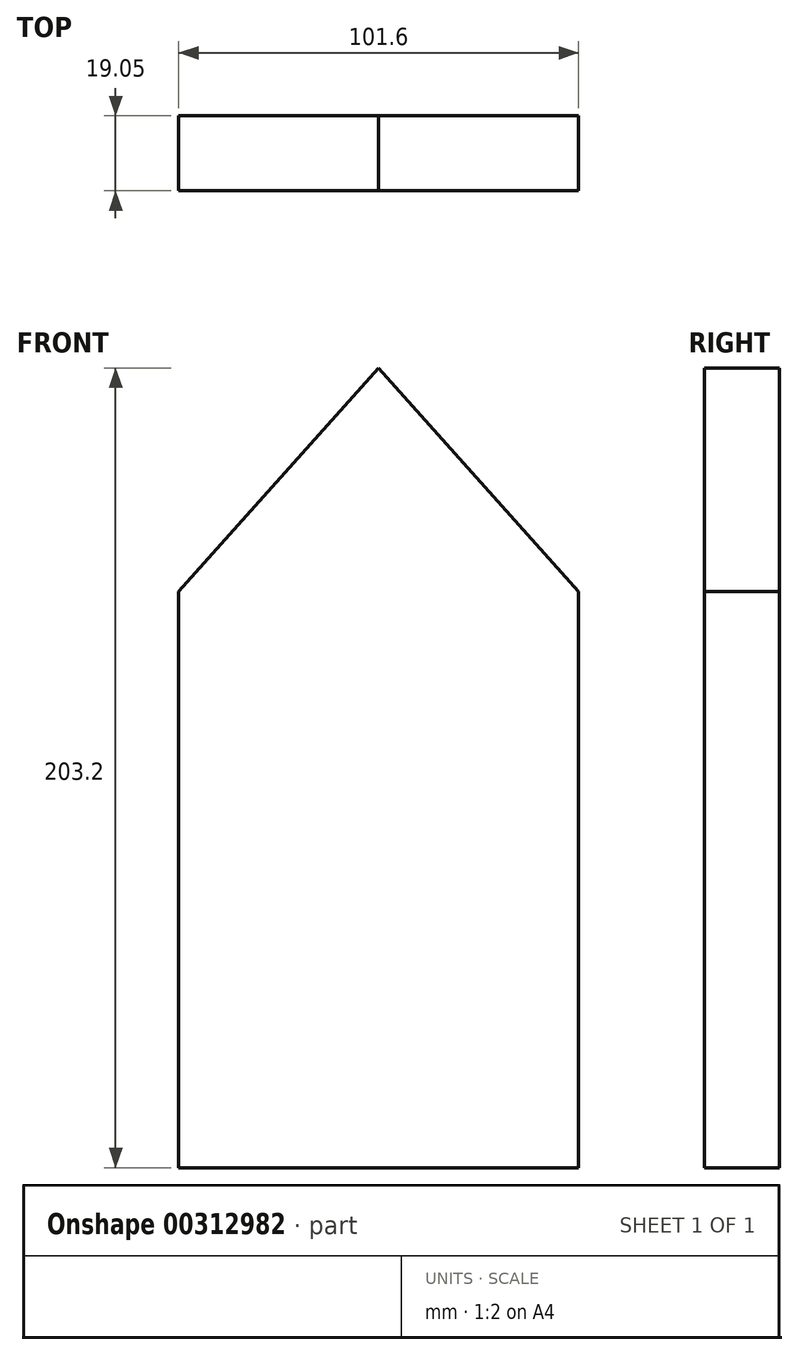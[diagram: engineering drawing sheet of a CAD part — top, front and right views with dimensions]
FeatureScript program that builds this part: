
annotation { "Feature Type Name" : "Feature", "Feature Type Description" : "" }
export const myFeature = defineFeature(function(context is Context, id is Id, definition is map)
    precondition{}
    {
        {
            var Q0;
            Q0=qCreatedBy(makeId("Front.planeOp"),FACE);
            var sketch = newSketch(context, id + "F0", { "sketchPlane" : qUnion([Q0])});
            skLineSegment(sketch, "E0.bottom", {"start": v(50.8, 101.6) * mm, "end": v(-50.8, 101.6) * mm});
            skLineSegment(sketch, "E0.top", {"start": v(50.8, -101.6) * mm, "end": v(-50.8, -101.6) * mm});
            skLineSegment(sketch, "E0.left", {"start": v(50.8, 101.6) * mm, "end": v(50.8, -101.6) * mm});
            skLineSegment(sketch, "E0.right", {"start": v(-50.8, 101.6) * mm, "end": v(-50.8, -101.6) * mm});
            skPoint(sketch, "E0.middle", {"position": v(0, 0) * mm});
            skSolve(sketch);
        }
        {
            var Q0;
            Q0 = qSketchRegion(id + "F0", true);
            extrude(context, id + "F1", {"entities" : qUnion([Q0]), "depth" : 19.05 * mm});
        }
        {
            var Q0;
            Q0=makeQuery(id+"F1.opExtrude","CAP_FACE",FACE,{"disambiguationData":[OSD([sQuery(id+"F0.wireOp",EDGE,"E0.bottom"),sQuery(id+"F0.wireOp",EDGE,"E0.top"),sQuery(id+"F0.wireOp",EDGE,"E0.left"),sQuery(id+"F0.wireOp",EDGE,"E0.right")])],"isStart":false});
            var sketch = newSketch(context, id + "F2", { "sketchPlane" : qUnion([Q0])});
            skLineSegment(sketch, "E1", {"start": v(0, 101.6) * mm, "end": v(-50.8, 44.8) * mm});
            skLineSegment(sketch, "E2", {"start": v(0, 101.6) * mm, "end": v(50.8, 44.8) * mm});
            skSolve(sketch);
        }
        {
            var Q0;
            Q0 = qSketchRegion(id + "F2", true);
            var Q1;
            {var subQ0=sQuery(id+"F2.wireOp",EDGE,"E1");Q1=makeQuery(id+"F2.imprint","IMPRINT",FACE,{"disambiguationData":[TD([[makeQuery(id+"F2.imprint","IMPRINT",EDGE,{"derivedFrom":subQ0}),-1.0]])]});}
            var Q2;
            {var subQ0=sQuery(id+"F2.wireOp",EDGE,"E2");Q2=makeQuery(id+"F2.imprint","IMPRINT",FACE,{"disambiguationData":[TD([[makeQuery(id+"F2.imprint","IMPRINT",EDGE,{"derivedFrom":subQ0}),1.0]])]});}
            extrude(context, id + "F3", {"entities" : qUnion([Q0, Q1, Q2]), "operationType" : NewBodyOperationType.REMOVE, "endBound" : BoundingType.THROUGH_ALL, "oppositeDirection" : true, "depth" : 25.4 * mm});
        }
    });
